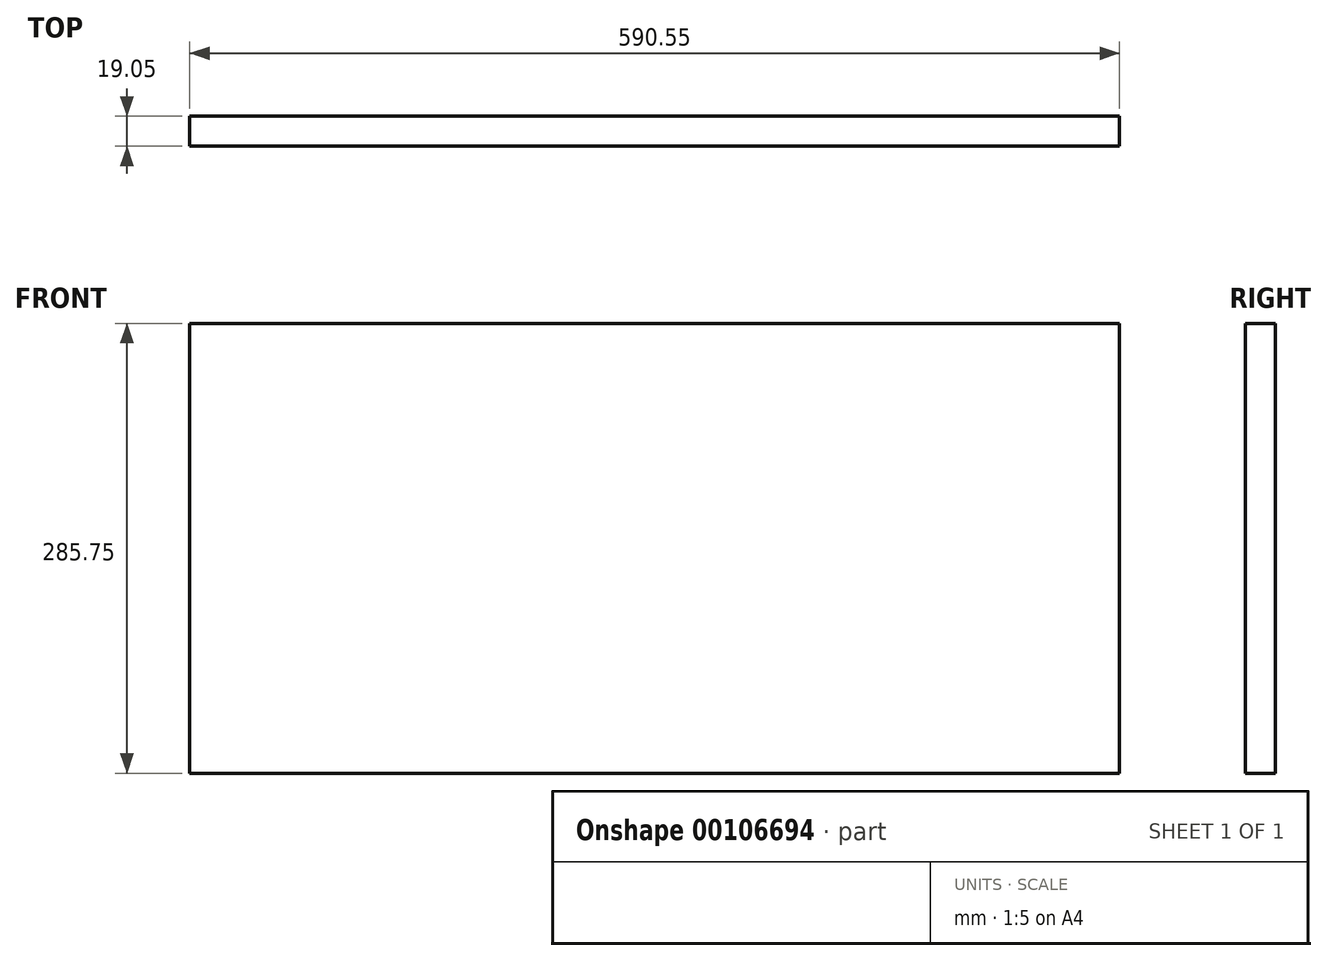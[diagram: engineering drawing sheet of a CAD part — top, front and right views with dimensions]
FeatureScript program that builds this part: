
annotation { "Feature Type Name" : "Feature", "Feature Type Description" : "" }
export const myFeature = defineFeature(function(context is Context, id is Id, definition is map)
    precondition{}
    {
        {
            var Q0;
            Q0=qCreatedBy(makeId("Front.planeOp"),FACE);
            var sketch = newSketch(context, id + "F0", { "sketchPlane" : qUnion([Q0])});
            skLineSegment(sketch, "E0.bottom", {"start": v(0, 0) * mm, "end": v(590.55, 0) * mm});
            skLineSegment(sketch, "E0.top", {"start": v(0, 285.75) * mm, "end": v(590.55, 285.75) * mm});
            skLineSegment(sketch, "E0.left", {"start": v(0, 0) * mm, "end": v(0, 285.75) * mm});
            skLineSegment(sketch, "E0.right", {"start": v(590.55, 0) * mm, "end": v(590.55, 285.75) * mm});
            skSolve(sketch);
        }
        {
            var Q0;
            Q0=makeQuery(id+"F0.imprint","IMPRINT",FACE,{"disambiguationData":[TD([[makeQuery(id+"F0.imprint","IMPRINT",EDGE,{"derivedFrom":sQuery(id+"F0.wireOp",EDGE,"E0.bottom")}),1.0]])]});
            extrude(context, id + "F1", {"entities" : qUnion([Q0]), "depth" : 19.05 * mm});
        }
    });
